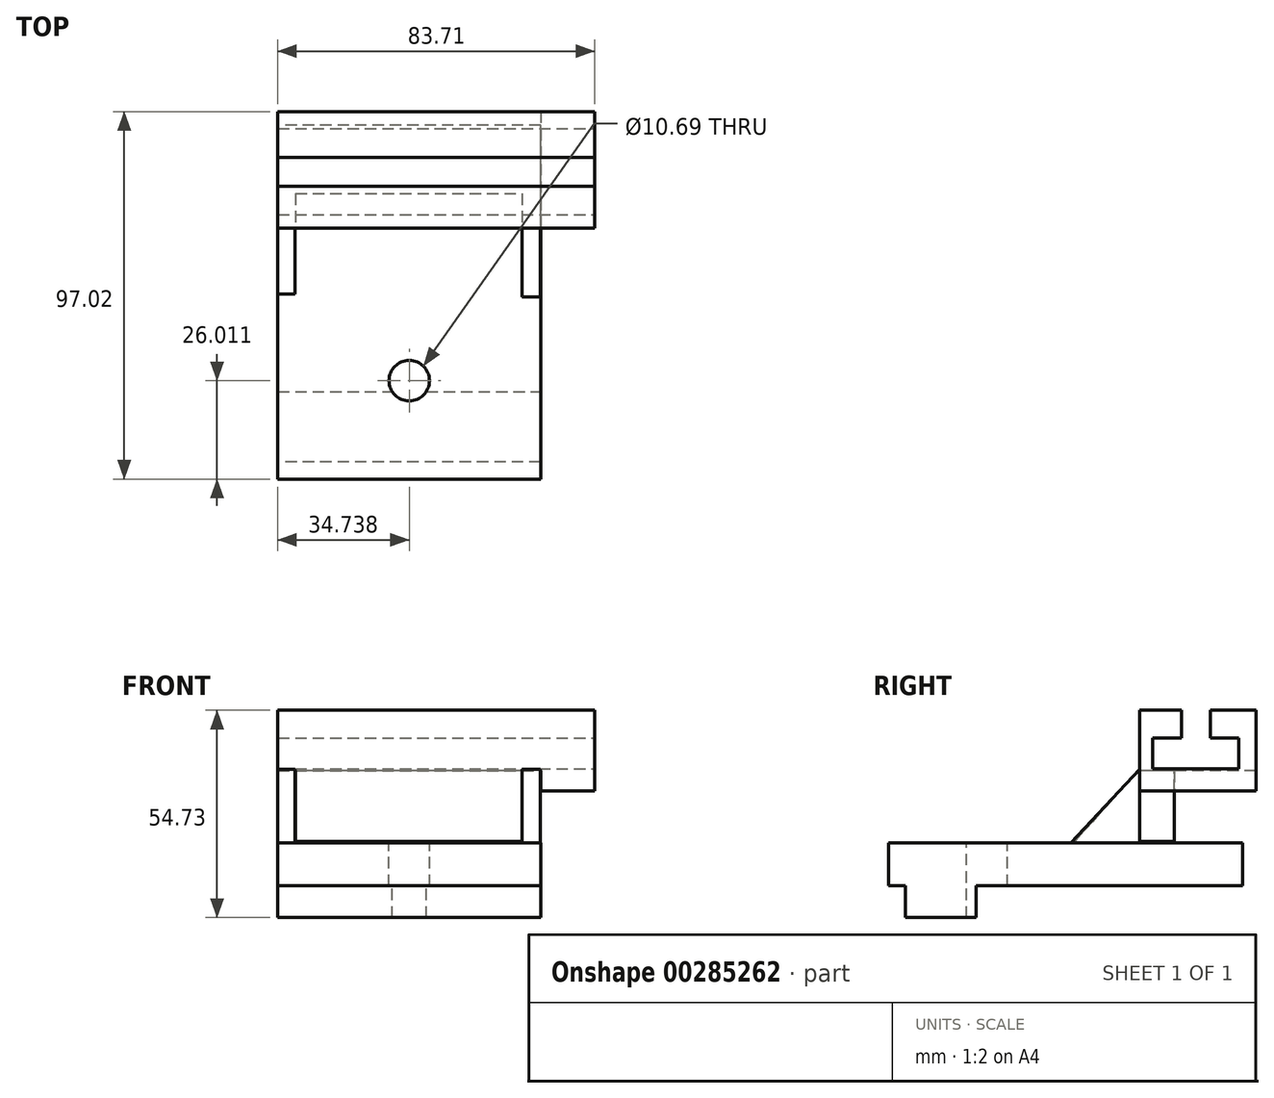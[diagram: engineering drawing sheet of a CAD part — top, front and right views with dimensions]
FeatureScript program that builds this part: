
annotation { "Feature Type Name" : "Feature", "Feature Type Description" : "" }
export const myFeature = defineFeature(function(context is Context, id is Id, definition is map)
    precondition{}
    {
        {
            var Q0;
            Q0=qCreatedBy(makeId("Front.planeOp"),FACE);
            var sketch = newSketch(context, id + "F0", { "sketchPlane" : qUnion([Q0])});
            skLineSegment(sketch, "E0", {"start": v(-48.97, 17.05) * mm, "end": v(20.4, 17.05) * mm});
            skLineSegment(sketch, "E1", {"start": v(20.4, 17.05) * mm, "end": v(20.4, 5.68) * mm});
            skLineSegment(sketch, "E2", {"start": v(20.4, 5.68) * mm, "end": v(-48.97, 5.68) * mm});
            skLineSegment(sketch, "E3", {"start": v(-48.97, 5.68) * mm, "end": v(-48.97, 17.05) * mm});
            skSolve(sketch);
        }
        {
            var Q0;
            Q0 = qSketchRegion(id + "F0", true);
            extrude(context, id + "F1", {"entities" : qUnion([Q0]), "depth" : 66.3 * mm});
        }
        {
            var Q0;
            Q0=makeQuery(id+"F1.opExtrude","SWEPT_FACE",FACE,{"disambiguationData":[OSD([sQuery(id+"F0.wireOp",EDGE,"E2")])]});
            var sketch = newSketch(context, id + "F2", { "sketchPlane" : qUnion([Q0])});
            skLineSegment(sketch, "E4", {"start": v(20.4, 61.8) * mm, "end": v(-48.97, 61.8) * mm});
            skLineSegment(sketch, "E5", {"start": v(-48.97, 61.8) * mm, "end": v(-48.97, 43.14) * mm});
            skLineSegment(sketch, "E6", {"start": v(-48.97, 43.14) * mm, "end": v(20.4, 43.14) * mm});
            skLineSegment(sketch, "E7", {"start": v(20.4, 43.14) * mm, "end": v(20.4, 61.8) * mm});
            skSolve(sketch);
        }
        {
            var Q0;
            Q0 = qSketchRegion(id + "F2", true);
            extrude(context, id + "F3", {"entities" : qUnion([Q0]), "operationType" : NewBodyOperationType.ADD, "depth" : 8.38 * mm});
        }
        {
            var Q0;
            Q0=qCreatedBy(makeId("Right.planeOp"),FACE);
            var sketch = newSketch(context, id + "F4", { "sketchPlane" : qUnion([Q0])});
            skLineSegment(sketch, "E8", {"start": v(0, 17.05) * mm, "end": v(0, 36.45) * mm});
            skLineSegment(sketch, "E9", {"start": v(0, 36.45) * mm, "end": v(-17.43, 17.05) * mm});
            skLineSegment(sketch, "E10", {"start": v(-17.43, 17.05) * mm, "end": v(0, 17.05) * mm});
            skSolve(sketch);
        }
        {
            var Q0;
            Q0 = qSketchRegion(id + "F4", true);
            extrude(context, id + "F5", {"entities" : qUnion([Q0]), "oppositeDirection" : true, "depth" : 49.02 * mm});
        }
        {
            var Q0;
            Q0=makeQuery(id+"F5.opExtrude","CAP_FACE",FACE,{"disambiguationData":[OSD([sQuery(id+"F4.wireOp",EDGE,"E8"),sQuery(id+"F4.wireOp",EDGE,"E9"),sQuery(id+"F4.wireOp",EDGE,"E10")])],"isStart":true});
            extrude(context, id + "F6", {"entities" : qUnion([Q0]), "operationType" : NewBodyOperationType.REMOVE, "oppositeDirection" : true, "depth" : 44.45 * mm});
        }
        {
            var Q0;
            Q0=qCreatedBy(makeId("Right.planeOp"),FACE);
            var sketch = newSketch(context, id + "F7", { "sketchPlane" : qUnion([Q0])});
            skLineSegment(sketch, "E11", {"start": v(0, 36.4) * mm, "end": v(0, 16.76) * mm});
            skLineSegment(sketch, "E12", {"start": v(0, 16.76) * mm, "end": v(-18.42, 16.76) * mm});
            skLineSegment(sketch, "E13", {"start": v(-18.42, 16.76) * mm, "end": v(0, 36.4) * mm});
            skSolve(sketch);
        }
        {
            var Q0;
            Q0=qCreatedBy(makeId("Front.planeOp"),FACE);
            var sketch = newSketch(context, id + "F8", { "sketchPlane" : qUnion([Q0])});
            skLineSegment(sketch, "E14", {"start": v(-48.97, 36) * mm, "end": v(-44.3, 36) * mm});
            skLineSegment(sketch, "E15", {"start": v(-44.3, 36) * mm, "end": v(-44.3, 17.34) * mm});
            skLineSegment(sketch, "E16", {"start": v(-44.3, 17.34) * mm, "end": v(15.45, 17.34) * mm});
            skLineSegment(sketch, "E17", {"start": v(15.45, 17.34) * mm, "end": v(15.45, 36) * mm});
            skLineSegment(sketch, "E18", {"start": v(15.45, 36) * mm, "end": v(20.4, 36) * mm});
            skLineSegment(sketch, "E19", {"start": v(20.4, 36) * mm, "end": v(20.4, 30.75) * mm});
            skLineSegment(sketch, "E20", {"start": v(15.45, 36) * mm, "end": v(-44.3, 36) * mm});
            skLineSegment(sketch, "E21", {"start": v(20.4, 30.75) * mm, "end": v(34.69, 30.75) * mm});
            skLineSegment(sketch, "E22", {"start": v(34.69, 30.75) * mm, "end": v(34.69, 52.03) * mm});
            skLineSegment(sketch, "E23", {"start": v(34.69, 52.03) * mm, "end": v(-48.97, 52.03) * mm});
            skLineSegment(sketch, "E24", {"start": v(-48.97, 52.03) * mm, "end": v(-48.97, 36) * mm});
            skSolve(sketch);
        }
        {
            var Q0;
            Q0 = qSketchRegion(id + "F7", true);
            extrude(context, id + "F9", {"entities" : qUnion([Q0]), "depth" : 20.32 * mm});
        }
        {
            var Q0;
            Q0=makeQuery(id+"F1.opExtrude","CAP_FACE",FACE,{"disambiguationData":[OSD([sQuery(id+"F0.wireOp",EDGE,"E0"),sQuery(id+"F0.wireOp",EDGE,"E1"),sQuery(id+"F0.wireOp",EDGE,"E2"),sQuery(id+"F0.wireOp",EDGE,"E3")])],"isStart":true});
            var sketch = newSketch(context, id + "F10", { "sketchPlane" : qUnion([Q0])});
            skSolve(sketch);
        }
        {
            var Q0;
            Q0 = qSketchRegion(id + "F10", true);
            var Q1;
            Q1=makeQuery(id+"F10.imprint","IMPRINT",FACE,{"disambiguationData":[TD([[makeQuery(id+"F10.imprint","IMPRINT",EDGE,{"derivedFrom":makeQuery(id+"F1.opExtrude","CAP_EDGE",EDGE,{"disambiguationData":[OSD([sQuery(id+"F0.wireOp",EDGE,"E0")])],"isStart":true})}),1.0]])]});
            extrude(context, id + "F11", {"entities" : qUnion([Q0, Q1]), "operationType" : NewBodyOperationType.ADD, "depth" : 27.18 * mm});
        }
        {
            var Q0;
            Q0=makeQuery(id+"F9.opExtrude","CAP_FACE",FACE,{"disambiguationData":[OSD([sQuery(id+"F7.wireOp",EDGE,"E11"),sQuery(id+"F7.wireOp",EDGE,"E12"),sQuery(id+"F7.wireOp",EDGE,"E13")])],"isStart":true});
            extrude(context, id + "F12", {"entities" : qUnion([Q0]), "operationType" : NewBodyOperationType.REMOVE, "oppositeDirection" : true, "depth" : 15.5 * mm});
        }
        {
            var Q0;
            {var subQ0=sQuery(id+"F0.wireOp",EDGE,"E0");Q0=makeQuery(id+"F11.boolean.opBoolean","MERGE",FACE,{"derivedFrom":[makeQuery(id+"F1.opExtrude","SWEPT_FACE",FACE,{"disambiguationData":[OSD([subQ0])]}),makeQuery(id+"F11.opExtrude","SWEPT_FACE",FACE,{"disambiguationData":[OSD([subQ0])]})]});}
            var sketch = newSketch(context, id + "F13", { "sketchPlane" : qUnion([Q0])});
            skCircle(sketch, "E25", {"center": v(-14.28, -40.28) * mm, "radius": 5.34 * mm});
            skPoint(sketch, "E25.centerSnap0", {"position": v(-14.28, -66.3) * mm});
            skSolve(sketch);
        }
        {
            var Q0;
            Q0 = qSketchRegion(id + "F13", true);
            extrude(context, id + "F14", {"entities" : qUnion([Q0]), "operationType" : NewBodyOperationType.REMOVE, "oppositeDirection" : true, "depth" : 25.4 * mm});
        }
        {
            var Q0;
            Q0 = qSketchRegion(id + "F8", true);
            extrude(context, id + "F15", {"entities" : qUnion([Q0]), "oppositeDirection" : true, "depth" : 30.73 * mm});
        }
        {
            var Q0;
            Q0=makeQuery(id+"F15.opExtrude","CAP_FACE",FACE,{"disambiguationData":[OSD([sQuery(id+"F8.wireOp",EDGE,"E14"),sQuery(id+"F8.wireOp",EDGE,"E15"),sQuery(id+"F8.wireOp",EDGE,"E16"),sQuery(id+"F8.wireOp",EDGE,"E17"),sQuery(id+"F8.wireOp",EDGE,"E18"),sQuery(id+"F8.wireOp",EDGE,"E19"),sQuery(id+"F8.wireOp",EDGE,"E21"),sQuery(id+"F8.wireOp",EDGE,"E22"),sQuery(id+"F8.wireOp",EDGE,"E23"),sQuery(id+"F8.wireOp",EDGE,"E24")])],"isStart":false});
            var sketch = newSketch(context, id + "F16", { "sketchPlane" : qUnion([Q0])});
            skLineSegment(sketch, "E26", {"start": v(-15.45, 36) * mm, "end": v(44.3, 36) * mm});
            skSolve(sketch);
        }
        {
            var Q0;
            Q0 = qSketchRegion(id + "F16", true);
            var Q1;
            Q1=makeQuery(id+"F16.imprint","IMPRINT",FACE,{"disambiguationData":[TD([[makeQuery(id+"F16.imprint","IMPRINT",EDGE,{"derivedFrom":sQuery(id+"F16.wireOp",EDGE,"E26")}),-1.0]])]});
            extrude(context, id + "F17", {"entities" : qUnion([Q0, Q1]), "operationType" : NewBodyOperationType.REMOVE, "oppositeDirection" : true, "depth" : 21.59 * mm});
        }
        {
            var Q0;
            Q0=makeQuery(id+"F15.opExtrude","SWEPT_FACE",FACE,{"disambiguationData":[OSD([sQuery(id+"F8.wireOp",EDGE,"E22")])]});
            var sketch = newSketch(context, id + "F18", { "sketchPlane" : qUnion([Q0])});
            skLineSegment(sketch, "E27", {"start": v(11.08, 52.03) * mm, "end": v(11.08, 44.74) * mm});
            skLineSegment(sketch, "E28", {"start": v(11.08, 44.74) * mm, "end": v(3.5, 44.74) * mm});
            skLineSegment(sketch, "E29", {"start": v(3.5, 44.74) * mm, "end": v(3.5, 36.58) * mm});
            skLineSegment(sketch, "E30", {"start": v(3.5, 36.58) * mm, "end": v(26.23, 36.58) * mm});
            skLineSegment(sketch, "E31", {"start": v(26.23, 36.58) * mm, "end": v(26.23, 44.74) * mm});
            skLineSegment(sketch, "E32", {"start": v(26.23, 44.74) * mm, "end": v(18.65, 44.74) * mm});
            skLineSegment(sketch, "E33", {"start": v(18.65, 44.74) * mm, "end": v(18.65, 52.03) * mm});
            skSolve(sketch);
        }
        {
            var Q0;
            {var subQ0=sQuery(id+"F18.wireOp",EDGE,"E27");Q0=makeQuery(id+"F18.imprint","IMPRINT",FACE,{"disambiguationData":[TD([[makeQuery(id+"F18.imprint","IMPRINT",EDGE,{"derivedFrom":subQ0}),1.0]])]});}
            var Q1;
            Q1 = qConstructionFilter(qBodyType(qCreatedBy(id + "F18" ,EDGE), BodyType.WIRE), ConstructionObject.NO);
            extrude(context, id + "F19", {"entities" : qUnion([Q0]), "operationType" : NewBodyOperationType.REMOVE, "surfaceEntities" : qUnion([Q1]), "oppositeDirection" : true, "depth" : 126.5 * mm});
        }
    });
